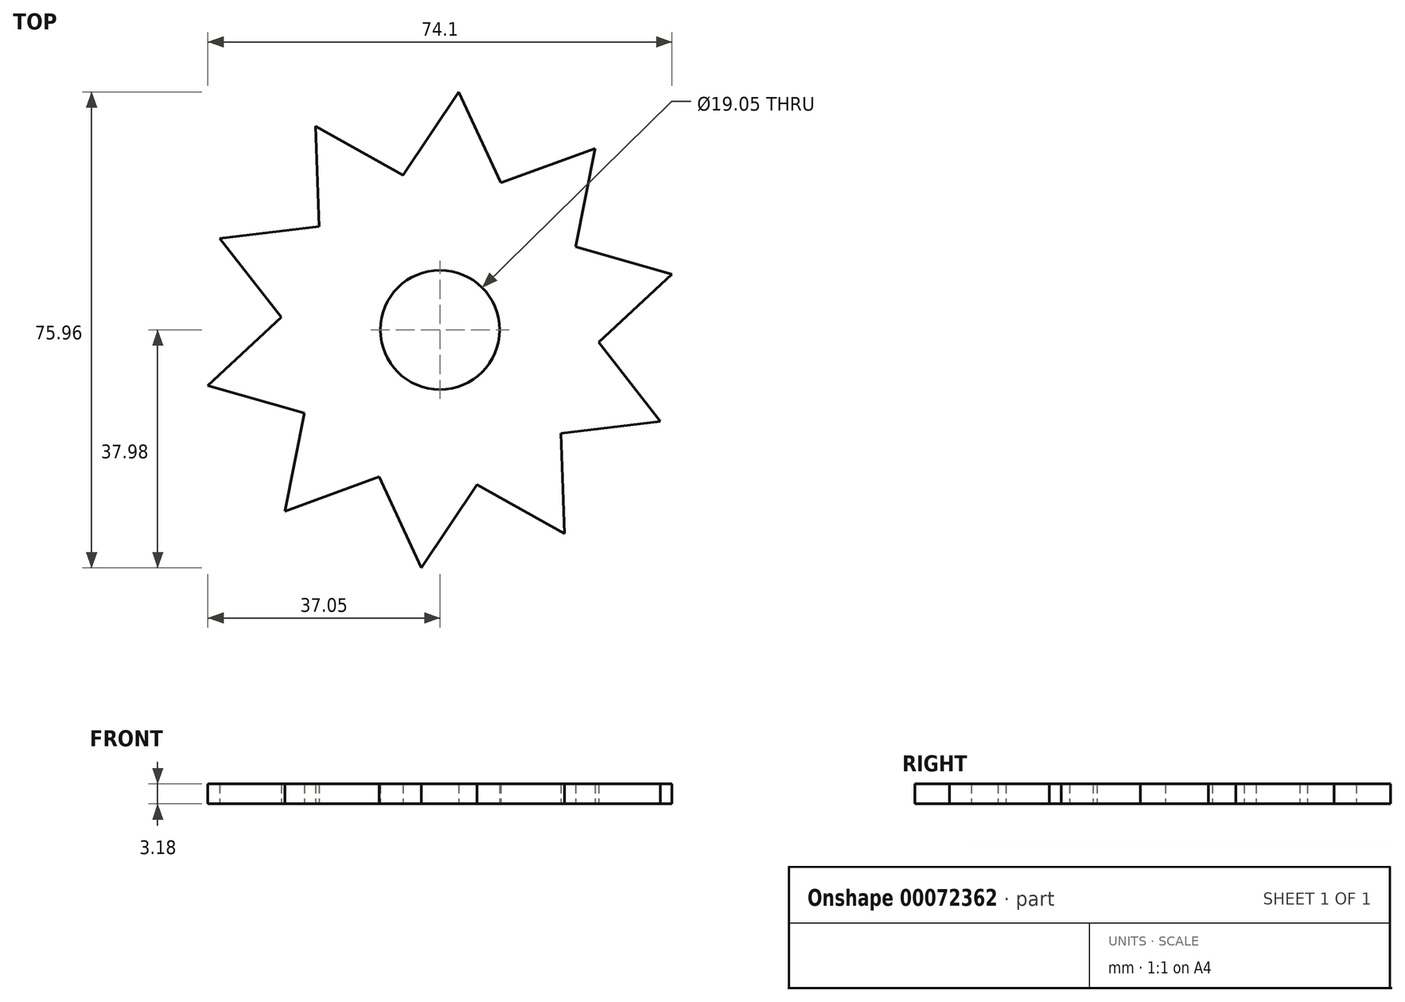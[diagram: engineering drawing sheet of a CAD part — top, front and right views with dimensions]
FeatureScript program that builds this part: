
annotation { "Feature Type Name" : "Feature", "Feature Type Description" : "" }
export const myFeature = defineFeature(function(context is Context, id is Id, definition is map)
    precondition{}
    {
        {
            var Q0;
            Q0=qCreatedBy(makeId("Top.planeOp"),FACE);
            var sketch = newSketch(context, id + "F0", { "sketchPlane" : qUnion([Q0])});
            skLineSegment(sketch, "E0", {"start": v(9.73, 23.46) * mm, "end": v(24.75, 28.96) * mm});
            skLineSegment(sketch, "E1", {"start": v(24.75, 28.96) * mm, "end": v(21.66, 13.26) * mm});
            skLineSegment(sketch, "E2.1.0", {"start": v(-5.92, 24.7) * mm, "end": v(3, 37.98) * mm});
            skLineSegment(sketch, "E2.1.1", {"start": v(3, 37.98) * mm, "end": v(9.73, 23.46) * mm});
            skLineSegment(sketch, "E2.2.0", {"start": v(-19.3, 16.5) * mm, "end": v(-19.9, 32.5) * mm});
            skLineSegment(sketch, "E2.2.1", {"start": v(-19.9, 32.5) * mm, "end": v(-5.92, 24.7) * mm});
            skLineSegment(sketch, "E2.3.0", {"start": v(-25.32, 2) * mm, "end": v(-35.2, 14.6) * mm});
            skLineSegment(sketch, "E2.3.1", {"start": v(-35.2, 14.6) * mm, "end": v(-19.3, 16.5) * mm});
            skLineSegment(sketch, "E2.4.0", {"start": v(-21.66, -13.26) * mm, "end": v(-37.05, -8.88) * mm});
            skLineSegment(sketch, "E2.4.1", {"start": v(-37.05, -8.88) * mm, "end": v(-25.32, 2) * mm});
            skLineSegment(sketch, "E2.5.0", {"start": v(-9.73, -23.46) * mm, "end": v(-24.75, -28.96) * mm});
            skLineSegment(sketch, "E2.5.1", {"start": v(-24.75, -28.96) * mm, "end": v(-21.66, -13.26) * mm});
            skLineSegment(sketch, "E2.6.0", {"start": v(5.92, -24.7) * mm, "end": v(-3, -37.98) * mm});
            skLineSegment(sketch, "E2.6.1", {"start": v(-3, -37.98) * mm, "end": v(-9.73, -23.46) * mm});
            skLineSegment(sketch, "E2.7.0", {"start": v(19.3, -16.5) * mm, "end": v(19.9, -32.5) * mm});
            skLineSegment(sketch, "E2.7.1", {"start": v(19.9, -32.5) * mm, "end": v(5.92, -24.7) * mm});
            skLineSegment(sketch, "E2.8.0", {"start": v(25.32, -2) * mm, "end": v(35.2, -14.6) * mm});
            skLineSegment(sketch, "E2.8.1", {"start": v(35.2, -14.6) * mm, "end": v(19.3, -16.5) * mm});
            skLineSegment(sketch, "E2.9.0", {"start": v(21.66, 13.26) * mm, "end": v(37.05, 8.88) * mm});
            skLineSegment(sketch, "E2.9.1", {"start": v(37.05, 8.88) * mm, "end": v(25.32, -2) * mm});
            skPoint(sketch, "E2.center", {"position": v(0, 0) * mm});
            skCircle(sketch, "E3", {"center": v(0, 0) * mm, "radius": 9.53 * mm});
            skSolve(sketch);
        }
        {
            var Q0;
            Q0=makeQuery(id+"F0.imprint","IMPRINT",FACE,{"disambiguationData":[TD([[makeQuery(id+"F0.imprint","IMPRINT",EDGE,{"derivedFrom":sQuery(id+"F0.wireOp",EDGE,"E0")}),-1.0]])]});
            extrude(context, id + "F1", {"entities" : qUnion([Q0]), "depth" : 3.17 * mm});
        }
    });
